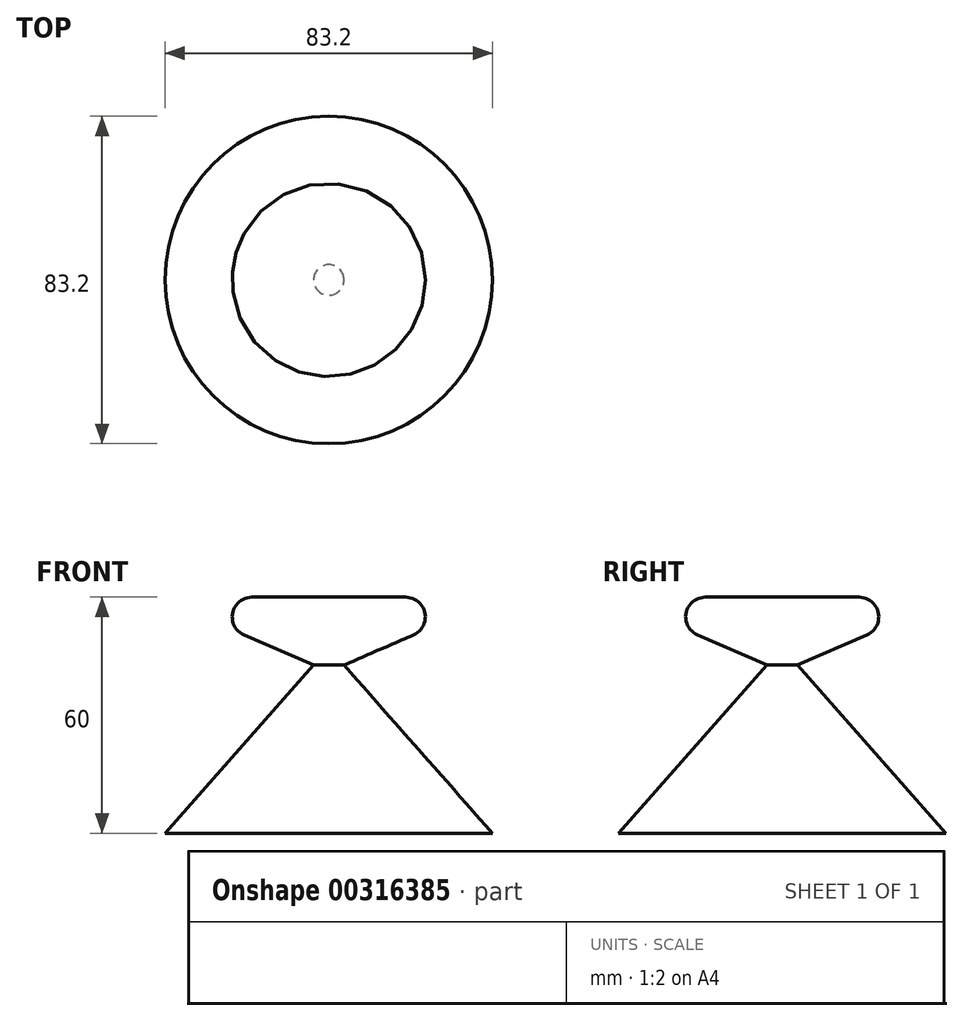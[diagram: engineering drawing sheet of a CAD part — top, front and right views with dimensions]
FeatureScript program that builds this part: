
annotation { "Feature Type Name" : "Feature", "Feature Type Description" : "" }
export const myFeature = defineFeature(function(context is Context, id is Id, definition is map)
    precondition{}
    {
        {
            var Q0;
            Q0=qCreatedBy(makeId("Front.planeOp"),FACE);
            var sketch = newSketch(context, id + "F0", { "sketchPlane" : qUnion([Q0])});
            skLineSegment(sketch, "E0", {"start": v(0, 0) * mm, "end": v(0, 60) * mm});
            skLineSegment(sketch, "E1", {"start": v(0, 60) * mm, "end": v(19.52, 60) * mm});
            skLineSegment(sketch, "E2", {"start": v(21.52, 50.42) * mm, "end": v(3.87, 42.73) * mm});
            skLineSegment(sketch, "E3", {"start": v(3.87, 42.73) * mm, "end": v(41.6, 0) * mm});
            skLineSegment(sketch, "E4", {"start": v(41.6, 0) * mm, "end": v(0, 0) * mm});
            skPoint(sketch, "E5.visualSharp", {"position": v(43.52, 60) * mm});
            skArc(sketch, "E5.filletArc", {"start": v(21.52, 50.42) * mm, "mid": v(24.42, 56.02) * mm, "end": v(19.52, 60) * mm});
            skLineSegment(sketch, "E6", {"start": v(0, 74.45) * mm, "end": v(0, -36.3) * mm, "construction": true});
            skSolve(sketch);
        }
        {
            var Q0;
            Q0=makeQuery(id+"F0.imprint","IMPRINT",FACE,{"disambiguationData":[TD([[makeQuery(id+"F0.imprint","IMPRINT",EDGE,{"derivedFrom":sQuery(id+"F0.wireOp",EDGE,"E0")}),-1.0]])]});
            var Q1;
            Q1=sQuery(id+"F0.wireOp",EDGE,"E6");
            revolve(context, id + "F1", {"entities" : qUnion([Q0]), "axis" : qUnion([Q1]), "revolveType" : RevolveType.FULL});
        }
    });
